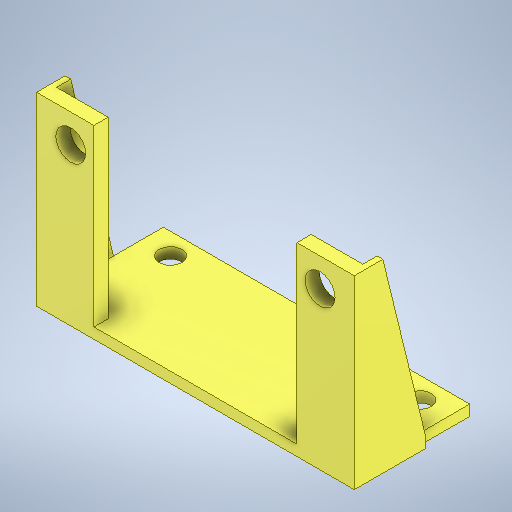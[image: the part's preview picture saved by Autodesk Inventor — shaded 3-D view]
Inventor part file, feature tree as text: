
AUTODESK INVENTOR PART (.ipt)
format: ipt  version: 2025.3 (Build 293356030, 356C)  size: 279,040 bytes
history: native  units: mm
features: sketch x3, extrude x3, other x1, hole x1, mirror x1
ambient origin geometry x8: Origin, YZ Plane, XZ Plane, XY Plane, X Axis, Y Axis, Z Axis, Center Point
bodies: Body1 (feature_tree)
feature tree (9):
  other  "ソリッド1"
  sketch  "スケッチ1"
  extrude  "前"  Depth=28.0mm
  extrude  "底"  Depth=1.5mm
  hole  "穴2"  [1 undecoded]
  extrude  "押し出し5"  Depth=4.2mm
  mirror  "ミラー3"
  sketch  "スケッチ5"
  sketch  "スケッチ6"
note: 1 required parameter value undecoded (feature->parameter linkage not recoverable at this tier; creation-order binding heuristic only, values carry confidence <= 0.55)
